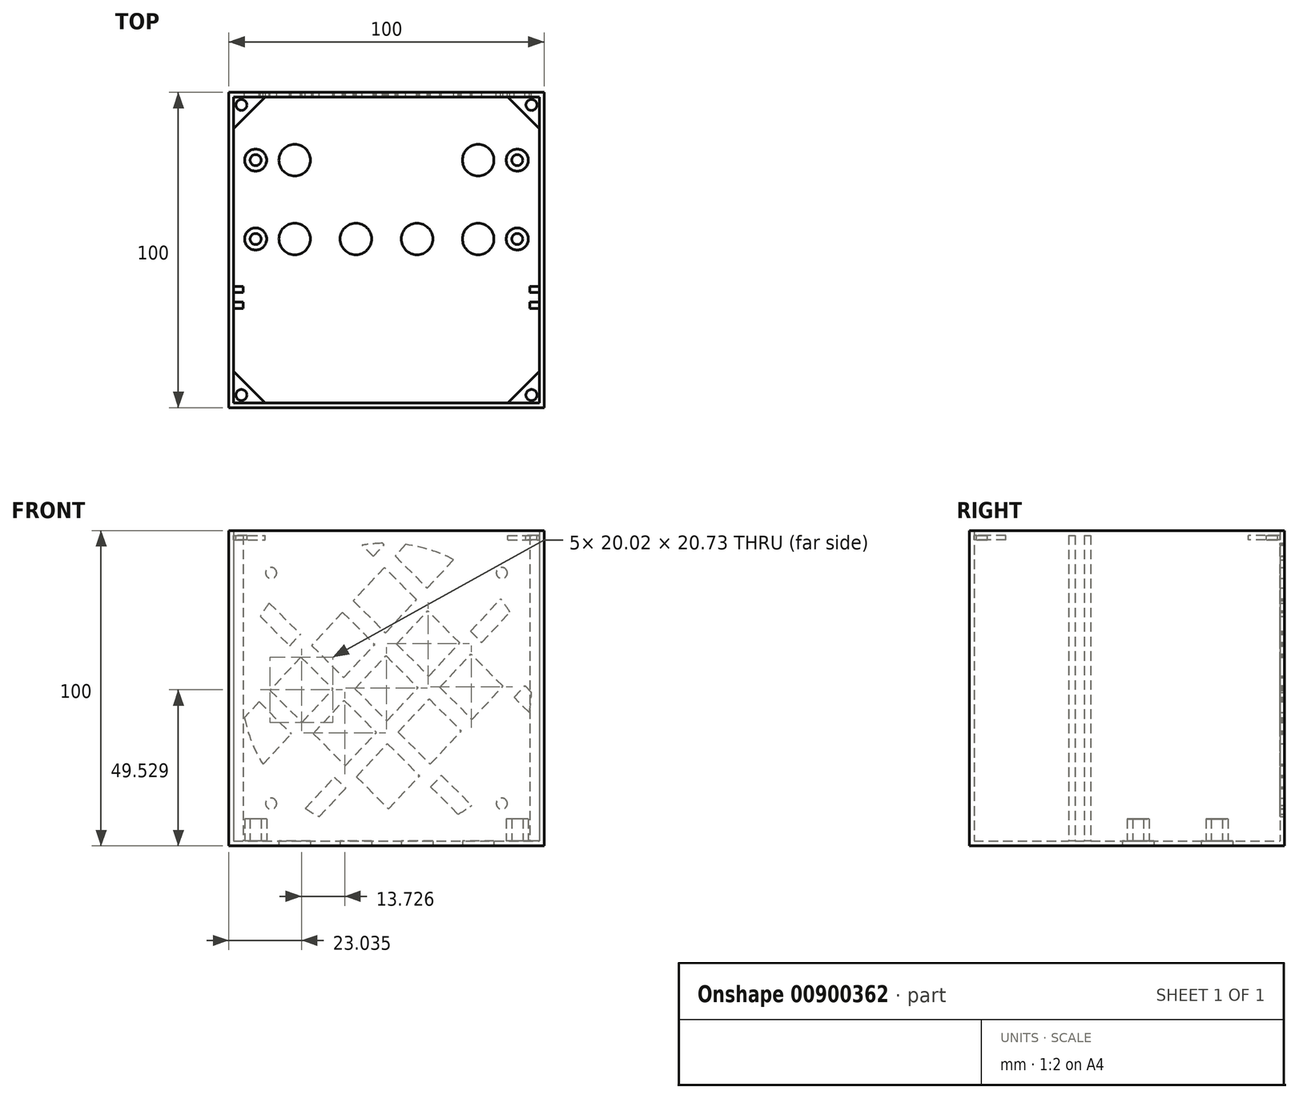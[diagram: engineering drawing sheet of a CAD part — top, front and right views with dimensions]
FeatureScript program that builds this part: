
annotation { "Feature Type Name" : "Feature", "Feature Type Description" : "" }
export const myFeature = defineFeature(function(context is Context, id is Id, definition is map)
    precondition{}
    {
        {
            var Q0;
            Q0=qCreatedBy(makeId("Top.planeOp"),FACE);
            var sketch = newSketch(context, id + "F0", { "sketchPlane" : qUnion([Q0])});
            skLineSegment(sketch, "E0.bottom", {"start": v(0, 0) * mm, "end": v(100, 0) * mm});
            skLineSegment(sketch, "E0.top", {"start": v(0, 100) * mm, "end": v(100, 100) * mm});
            skLineSegment(sketch, "E0.left", {"start": v(0, 0) * mm, "end": v(0, 100) * mm});
            skLineSegment(sketch, "E0.right", {"start": v(100, 0) * mm, "end": v(100, 100) * mm});
            skLineSegment(sketch, "E1.bottom", {"start": v(1.5, 1.5) * mm, "end": v(98.5, 1.5) * mm});
            skLineSegment(sketch, "E1.top", {"start": v(1.5, 98.5) * mm, "end": v(98.5, 98.5) * mm});
            skLineSegment(sketch, "E1.left", {"start": v(1.5, 1.5) * mm, "end": v(1.5, 98.5) * mm});
            skLineSegment(sketch, "E1.right", {"start": v(98.5, 1.5) * mm, "end": v(98.5, 98.5) * mm});
            skCircle(sketch, "E2", {"center": v(40.3, 53.5) * mm, "radius": 5 * mm});
            skCircle(sketch, "E3", {"center": v(59.7, 53.5) * mm, "radius": 5 * mm});
            skCircle(sketch, "E4", {"center": v(79.1, 53.5) * mm, "radius": 5 * mm});
            skCircle(sketch, "E5", {"center": v(20.9, 53.5) * mm, "radius": 5 * mm});
            skCircle(sketch, "E6", {"center": v(20.9, 78.5) * mm, "radius": 5 * mm});
            skCircle(sketch, "E7", {"center": v(79.1, 78.5) * mm, "radius": 5 * mm});
            skLineSegment(sketch, "E8", {"start": v(1.5, 53.5) * mm, "end": v(98.5, 53.5) * mm, "construction": true});
            skLineSegment(sketch, "E9.bottom", {"start": v(1.5, 38.5) * mm, "end": v(4.5, 38.5) * mm});
            skLineSegment(sketch, "E9.top", {"start": v(1.5, 36.5) * mm, "end": v(4.5, 36.5) * mm});
            skLineSegment(sketch, "E9.left", {"start": v(1.5, 38.5) * mm, "end": v(1.5, 36.5) * mm});
            skLineSegment(sketch, "E9.right", {"start": v(4.5, 38.5) * mm, "end": v(4.5, 36.5) * mm});
            skLineSegment(sketch, "E10.bottom", {"start": v(1.5, 33.5) * mm, "end": v(4.5, 33.5) * mm});
            skLineSegment(sketch, "E10.top", {"start": v(1.5, 31.5) * mm, "end": v(4.5, 31.5) * mm});
            skLineSegment(sketch, "E10.left", {"start": v(1.5, 33.5) * mm, "end": v(1.5, 31.5) * mm});
            skLineSegment(sketch, "E10.right", {"start": v(4.5, 33.5) * mm, "end": v(4.5, 31.5) * mm});
            skLineSegment(sketch, "E11.bottom", {"start": v(98.5, 38.5) * mm, "end": v(95.5, 38.5) * mm});
            skLineSegment(sketch, "E11.top", {"start": v(98.5, 36.5) * mm, "end": v(95.5, 36.5) * mm});
            skLineSegment(sketch, "E11.left", {"start": v(98.5, 38.5) * mm, "end": v(98.5, 36.5) * mm});
            skLineSegment(sketch, "E11.right", {"start": v(95.5, 38.5) * mm, "end": v(95.5, 36.5) * mm});
            skLineSegment(sketch, "E12.bottom", {"start": v(98.5, 33.5) * mm, "end": v(95.5, 33.5) * mm});
            skLineSegment(sketch, "E12.top", {"start": v(98.5, 31.5) * mm, "end": v(95.5, 31.5) * mm});
            skLineSegment(sketch, "E12.left", {"start": v(98.5, 33.5) * mm, "end": v(98.5, 31.5) * mm});
            skLineSegment(sketch, "E12.right", {"start": v(95.5, 33.5) * mm, "end": v(95.5, 31.5) * mm});
            skSolve(sketch);
        }
        {
            var Q0;
            Q0 = qSketchRegion(id + "F0", true);
            var Q1;
            Q1=makeQuery(id+"F0.imprint","IMPRINT",FACE,{"disambiguationData":[TD([[makeQuery(id+"F0.imprint","IMPRINT",EDGE,{"derivedFrom":sQuery(id+"F0.wireOp",EDGE,"E1.bottom")}),1.0]])]});
            var Q2;
            Q2=makeQuery(id+"F0.imprint","IMPRINT",FACE,{"disambiguationData":[TD([[makeQuery(id+"F0.imprint","IMPRINT",EDGE,{"derivedFrom":sQuery(id+"F0.wireOp",EDGE,"E9.bottom")}),-1.0]])]});
            var Q3;
            Q3=makeQuery(id+"F0.imprint","IMPRINT",FACE,{"disambiguationData":[TD([[makeQuery(id+"F0.imprint","IMPRINT",EDGE,{"derivedFrom":sQuery(id+"F0.wireOp",EDGE,"E10.bottom")}),-1.0]])]});
            var Q4;
            Q4=makeQuery(id+"F0.imprint","IMPRINT",FACE,{"disambiguationData":[TD([[makeQuery(id+"F0.imprint","IMPRINT",EDGE,{"derivedFrom":sQuery(id+"F0.wireOp",EDGE,"E11.bottom")}),1.0]])]});
            var Q5;
            Q5=makeQuery(id+"F0.imprint","IMPRINT",FACE,{"disambiguationData":[TD([[makeQuery(id+"F0.imprint","IMPRINT",EDGE,{"derivedFrom":sQuery(id+"F0.wireOp",EDGE,"E12.bottom")}),1.0]])]});
            extrude(context, id + "F1", {"entities" : qUnion([Q0, Q1, Q2, Q3, Q4, Q5]), "depth" : 1.5 * mm, "offsetDistance" : 25 * mm});
        }
        {
            var Q0;
            Q0=makeQuery(id+"F1.opExtrude","CAP_FACE",FACE,{"disambiguationData":[OSD([sQuery(id+"F0.wireOp",EDGE,"E0.bottom"),sQuery(id+"F0.wireOp",EDGE,"E0.top"),sQuery(id+"F0.wireOp",EDGE,"E0.left"),sQuery(id+"F0.wireOp",EDGE,"E0.right"),sQuery(id+"F0.wireOp",EDGE,"E2"),sQuery(id+"F0.wireOp",EDGE,"E3"),sQuery(id+"F0.wireOp",EDGE,"E4"),sQuery(id+"F0.wireOp",EDGE,"E5"),sQuery(id+"F0.wireOp",EDGE,"E6"),sQuery(id+"F0.wireOp",EDGE,"E7")])],"isStart":false});
            var sketch = newSketch(context, id + "F2", { "sketchPlane" : qUnion([Q0])});
            skLineSegment(sketch, "E13.bottom", {"start": v(0, 0) * mm, "end": v(100, 0) * mm});
            skLineSegment(sketch, "E13.top", {"start": v(0, 100) * mm, "end": v(100, 100) * mm});
            skLineSegment(sketch, "E13.left", {"start": v(0, 0) * mm, "end": v(0, 100) * mm});
            skLineSegment(sketch, "E13.right", {"start": v(100, 0) * mm, "end": v(100, 100) * mm});
            skLineSegment(sketch, "E14.bottom", {"start": v(1.5, 1.5) * mm, "end": v(98.5, 1.5) * mm});
            skLineSegment(sketch, "E14.top", {"start": v(1.5, 98.5) * mm, "end": v(98.5, 98.5) * mm});
            skLineSegment(sketch, "E14.left", {"start": v(1.5, 1.5) * mm, "end": v(1.5, 98.5) * mm});
            skLineSegment(sketch, "E14.right", {"start": v(98.5, 1.5) * mm, "end": v(98.5, 98.5) * mm});
            skCircle(sketch, "E15", {"center": v(40.3, 53.5) * mm, "radius": 5 * mm});
            skCircle(sketch, "E16", {"center": v(59.7, 53.5) * mm, "radius": 5 * mm});
            skCircle(sketch, "E17", {"center": v(79.1, 53.5) * mm, "radius": 5 * mm});
            skCircle(sketch, "E18", {"center": v(20.9, 53.5) * mm, "radius": 5 * mm});
            skCircle(sketch, "E19", {"center": v(20.9, 78.5) * mm, "radius": 5 * mm});
            skCircle(sketch, "E20", {"center": v(79.1, 78.5) * mm, "radius": 5 * mm});
            skLineSegment(sketch, "E21", {"start": v(1.5, 53.5) * mm, "end": v(98.5, 53.5) * mm, "construction": true});
            skLineSegment(sketch, "E22.bottom", {"start": v(1.5, 38.5) * mm, "end": v(4.5, 38.5) * mm});
            skLineSegment(sketch, "E22.top", {"start": v(1.5, 36.5) * mm, "end": v(4.5, 36.5) * mm});
            skLineSegment(sketch, "E22.left", {"start": v(1.5, 38.5) * mm, "end": v(1.5, 36.5) * mm});
            skLineSegment(sketch, "E22.right", {"start": v(4.5, 38.5) * mm, "end": v(4.5, 36.5) * mm});
            skLineSegment(sketch, "E23.bottom", {"start": v(1.5, 33.5) * mm, "end": v(4.5, 33.5) * mm});
            skLineSegment(sketch, "E23.top", {"start": v(1.5, 31.5) * mm, "end": v(4.5, 31.5) * mm});
            skLineSegment(sketch, "E23.left", {"start": v(1.5, 33.5) * mm, "end": v(1.5, 31.5) * mm});
            skLineSegment(sketch, "E23.right", {"start": v(4.5, 33.5) * mm, "end": v(4.5, 31.5) * mm});
            skLineSegment(sketch, "E24.bottom", {"start": v(98.5, 38.5) * mm, "end": v(95.5, 38.5) * mm});
            skLineSegment(sketch, "E24.top", {"start": v(98.5, 36.5) * mm, "end": v(95.5, 36.5) * mm});
            skLineSegment(sketch, "E24.left", {"start": v(98.5, 38.5) * mm, "end": v(98.5, 36.5) * mm});
            skLineSegment(sketch, "E24.right", {"start": v(95.5, 38.5) * mm, "end": v(95.5, 36.5) * mm});
            skLineSegment(sketch, "E25.bottom", {"start": v(98.5, 33.5) * mm, "end": v(95.5, 33.5) * mm});
            skLineSegment(sketch, "E25.top", {"start": v(98.5, 31.5) * mm, "end": v(95.5, 31.5) * mm});
            skLineSegment(sketch, "E25.left", {"start": v(98.5, 33.5) * mm, "end": v(98.5, 31.5) * mm});
            skLineSegment(sketch, "E25.right", {"start": v(95.5, 33.5) * mm, "end": v(95.5, 31.5) * mm});
            skCircle(sketch, "E26", {"center": v(8.5, 53.5) * mm, "radius": 1.75 * mm});
            skCircle(sketch, "E27", {"center": v(8.5, 53.5) * mm, "radius": 3.5 * mm});
            skCircle(sketch, "E28", {"center": v(91.5, 53.5) * mm, "radius": 1.75 * mm});
            skCircle(sketch, "E29", {"center": v(91.5, 53.5) * mm, "radius": 3.5 * mm});
            skLineSegment(sketch, "E30", {"start": v(1.5, 78.5) * mm, "end": v(98.5, 78.5) * mm, "construction": true});
            skCircle(sketch, "E31", {"center": v(8.5, 78.5) * mm, "radius": 1.75 * mm});
            skCircle(sketch, "E32", {"center": v(8.5, 78.5) * mm, "radius": 3.5 * mm});
            skCircle(sketch, "E33", {"center": v(91.5, 78.5) * mm, "radius": 1.75 * mm});
            skCircle(sketch, "E34", {"center": v(91.5, 78.5) * mm, "radius": 3.5 * mm});
            skSolve(sketch);
        }
        {
            var Q0;
            Q0=makeQuery(id+"F2.imprint","IMPRINT",FACE,{"disambiguationData":[TD([[makeQuery(id+"F2.imprint","IMPRINT",EDGE,{"derivedFrom":sQuery(id+"F2.wireOp",EDGE,"E13.bottom")}),1.0]])]});
            extrude(context, id + "F3", {"entities" : qUnion([Q0]), "operationType" : NewBodyOperationType.ADD, "depth" : 98.5 * mm, "offsetDistance" : 25 * mm});
        }
        {
            var Q0;
            Q0 = qSketchRegion(id + "F2", true);
            var Q1;
            Q1=makeQuery(id+"F2.imprint","IMPRINT",FACE,{"disambiguationData":[TD([[makeQuery(id+"F2.imprint","IMPRINT",EDGE,{"derivedFrom":sQuery(id+"F2.wireOp",EDGE,"E22.bottom")}),-1.0]])]});
            var Q2;
            Q2=makeQuery(id+"F2.imprint","IMPRINT",FACE,{"disambiguationData":[TD([[makeQuery(id+"F2.imprint","IMPRINT",EDGE,{"derivedFrom":sQuery(id+"F2.wireOp",EDGE,"E23.bottom")}),-1.0]])]});
            var Q3;
            Q3=makeQuery(id+"F2.imprint","IMPRINT",FACE,{"disambiguationData":[TD([[makeQuery(id+"F2.imprint","IMPRINT",EDGE,{"derivedFrom":sQuery(id+"F2.wireOp",EDGE,"E24.bottom")}),1.0]])]});
            var Q4;
            Q4=makeQuery(id+"F2.imprint","IMPRINT",FACE,{"disambiguationData":[TD([[makeQuery(id+"F2.imprint","IMPRINT",EDGE,{"derivedFrom":sQuery(id+"F2.wireOp",EDGE,"E25.bottom")}),1.0]])]});
            extrude(context, id + "F4", {"entities" : qUnion([Q0, Q1, Q2, Q3, Q4]), "operationType" : NewBodyOperationType.ADD, "depth" : 97 * mm, "offsetDistance" : 25 * mm});
        }
        {
            var Q0;
            Q0=makeQuery(id+"F3.boolean.opBoolean","MERGE",FACE,{"derivedFrom":[makeQuery(id+"F1.opExtrude","SWEPT_FACE",FACE,{"disambiguationData":[OSD([sQuery(id+"F0.wireOp",EDGE,"E0.top")])]}),makeQuery(id+"F3.opExtrude","SWEPT_FACE",FACE,{"disambiguationData":[OSD([sQuery(id+"F2.wireOp",EDGE,"E13.top")])]})]});
            var sketch = newSketch(context, id + "F5", { "sketchPlane" : qUnion([Q0])});
            skLineSegment(sketch, "E35.0", {"start": v(0, 0) * mm, "end": v(-100, 0) * mm});
            skLineSegment(sketch, "E36.0", {"start": v(0, 100) * mm, "end": v(-100, 100) * mm});
            skLineSegment(sketch, "E37", {"start": v(-50, 100) * mm, "end": v(-50, 0) * mm, "construction": true});
            skLineSegment(sketch, "E38", {"start": v(-100, 50) * mm, "end": v(0, 50) * mm, "construction": true});
            skCircle(sketch, "E39", {"center": v(-50, 50) * mm, "radius": 46 * mm});
            skLineSegment(sketch, "E40", {"start": v(-48.7, 95.98) * mm, "end": v(-95.98, 48.7) * mm});
            skLineSegment(sketch, "E41", {"start": v(-95.35, 42.27) * mm, "end": v(-42.27, 95.35) * mm});
            skLineSegment(sketch, "E42", {"start": v(-27.26, 89.99) * mm, "end": v(-89.99, 27.26) * mm});
            skLineSegment(sketch, "E43", {"start": v(-12.78, 77.03) * mm, "end": v(-77.03, 12.78) * mm});
            skLineSegment(sketch, "E44", {"start": v(-10.01, 72.74) * mm, "end": v(-72.74, 10.01) * mm});
            skLineSegment(sketch, "E45", {"start": v(-4.65, 57.73) * mm, "end": v(-57.73, 4.65) * mm});
            skLineSegment(sketch, "E46", {"start": v(-4.02, 51.3) * mm, "end": v(-51.3, 4.02) * mm});
            skLineSegment(sketch, "E47", {"start": v(-22.97, 87.22) * mm, "end": v(-87.22, 22.97) * mm});
            skLineSegment(sketch, "E48", {"start": v(-4.1, 47.1) * mm, "end": v(-49.69, 96) * mm});
            skLineSegment(sketch, "E49", {"start": v(-56.14, 95.59) * mm, "end": v(-4.95, 40.7) * mm});
            skLineSegment(sketch, "E50", {"start": v(-10.83, 25.88) * mm, "end": v(-71.32, 90.76) * mm});
            skLineSegment(sketch, "E51", {"start": v(-24.28, 11.86) * mm, "end": v(-86.25, 78.32) * mm});
            skLineSegment(sketch, "E52", {"start": v(-28.68, 9.24) * mm, "end": v(-89.17, 74.12) * mm});
            skLineSegment(sketch, "E53", {"start": v(-43.86, 4.41) * mm, "end": v(-95.05, 59.3) * mm});
            skLineSegment(sketch, "E54", {"start": v(-50.31, 4) * mm, "end": v(-95.9, 52.9) * mm});
            skLineSegment(sketch, "E55", {"start": v(-13.75, 21.68) * mm, "end": v(-75.72, 88.14) * mm});
            skLineSegment(sketch, "E56", {"start": v(0, 100) * mm, "end": v(-100, 0) * mm, "construction": true});
            skLineSegment(sketch, "E57", {"start": v(-100, 100) * mm, "end": v(0, 0) * mm, "construction": true});
            skCircle(sketch, "E58", {"center": v(-13.4, 86.6) * mm, "radius": 1.75 * mm});
            skCircle(sketch, "E59", {"center": v(-86.6, 86.6) * mm, "radius": 1.75 * mm});
            skCircle(sketch, "E60", {"center": v(-86.6, 13.4) * mm, "radius": 1.75 * mm});
            skCircle(sketch, "E61", {"center": v(-13.4, 13.4) * mm, "radius": 1.75 * mm});
            skSolve(sketch);
        }
        {
            var Q0;
            {var subQ0=sQuery(id+"F5.wireOp",EDGE,"E51");var subQ1=sQuery(id+"F5.wireOp",EDGE,"E39");var subQ2=makeQuery(id+"F5.imprint","INTERSECT",VERTEX,{"disambiguationData":[OD(1.0)],"derivedFrom":[subQ1,subQ0]});Q0=makeQuery(id+"F5.imprint","IMPRINT",FACE,{"disambiguationData":[TD([[makeQuery(id+"F5.imprint","IMPRINT",EDGE,{"disambiguationData":[TD([[subQ2,1.0]])],"derivedFrom":subQ1}),1.0]])]});}
            var Q1;
            {var subQ0=sQuery(id+"F5.wireOp",EDGE,"E49");var subQ1=sQuery(id+"F5.wireOp",EDGE,"E39");var subQ2=makeQuery(id+"F5.imprint","INTERSECT",VERTEX,{"disambiguationData":[OD(0.0)],"derivedFrom":[subQ1,subQ0]});Q1=makeQuery(id+"F5.imprint","IMPRINT",FACE,{"disambiguationData":[TD([[makeQuery(id+"F5.imprint","IMPRINT",EDGE,{"disambiguationData":[TD([[subQ2,-1.0]])],"derivedFrom":subQ1}),1.0]])]});}
            var Q2;
            {var subQ0=sQuery(id+"F5.wireOp",EDGE,"E41");var subQ1=sQuery(id+"F5.wireOp",EDGE,"E39");var subQ2=makeQuery(id+"F5.imprint","INTERSECT",VERTEX,{"disambiguationData":[OD(1.0)],"derivedFrom":[subQ1,subQ0]});Q2=makeQuery(id+"F5.imprint","IMPRINT",FACE,{"disambiguationData":[TD([[makeQuery(id+"F5.imprint","IMPRINT",EDGE,{"disambiguationData":[TD([[subQ2,1.0]])],"derivedFrom":subQ1}),1.0]])]});}
            var Q3;
            {var subQ0=sQuery(id+"F5.wireOp",EDGE,"E43");var subQ1=sQuery(id+"F5.wireOp",EDGE,"E39");var subQ2=makeQuery(id+"F5.imprint","INTERSECT",VERTEX,{"disambiguationData":[OD(0.0)],"derivedFrom":[subQ1,subQ0]});Q3=makeQuery(id+"F5.imprint","IMPRINT",FACE,{"disambiguationData":[TD([[makeQuery(id+"F5.imprint","IMPRINT",EDGE,{"disambiguationData":[TD([[subQ2,-1.0]])],"derivedFrom":subQ1}),1.0]])]});}
            var Q4;
            {var subQ0=sQuery(id+"F5.wireOp",EDGE,"E50");var subQ1=sQuery(id+"F5.wireOp",EDGE,"E41");var subQ2=makeQuery(id+"F5.imprint","INTERSECT",VERTEX,{"derivedFrom":[subQ1,subQ0]});Q4=makeQuery(id+"F5.imprint","IMPRINT",FACE,{"disambiguationData":[TD([[makeQuery(id+"F5.imprint","IMPRINT",EDGE,{"disambiguationData":[TD([[subQ2,-1.0]])],"derivedFrom":subQ1}),-1.0]])]});}
            var Q5;
            {var subQ0=sQuery(id+"F5.wireOp",EDGE,"E52");var subQ1=sQuery(id+"F5.wireOp",EDGE,"E39");var subQ2=makeQuery(id+"F5.imprint","INTERSECT",VERTEX,{"disambiguationData":[OD(1.0)],"derivedFrom":[subQ1,subQ0]});Q5=makeQuery(id+"F5.imprint","IMPRINT",FACE,{"disambiguationData":[TD([[makeQuery(id+"F5.imprint","IMPRINT",EDGE,{"disambiguationData":[TD([[subQ2,-1.0]])],"derivedFrom":subQ1}),1.0]])]});}
            var Q6;
            {var subQ0=sQuery(id+"F5.wireOp",EDGE,"E51");var subQ1=sQuery(id+"F5.wireOp",EDGE,"E41");var subQ2=makeQuery(id+"F5.imprint","INTERSECT",VERTEX,{"derivedFrom":[subQ1,subQ0]});Q6=makeQuery(id+"F5.imprint","IMPRINT",FACE,{"disambiguationData":[TD([[makeQuery(id+"F5.imprint","IMPRINT",EDGE,{"disambiguationData":[TD([[subQ2,-1.0]])],"derivedFrom":subQ1}),-1.0]])]});}
            var Q7;
            {var subQ0=sQuery(id+"F5.wireOp",EDGE,"E49");var subQ1=sQuery(id+"F5.wireOp",EDGE,"E43");var subQ2=makeQuery(id+"F5.imprint","INTERSECT",VERTEX,{"derivedFrom":[subQ1,subQ0]});Q7=makeQuery(id+"F5.imprint","IMPRINT",FACE,{"disambiguationData":[TD([[makeQuery(id+"F5.imprint","IMPRINT",EDGE,{"disambiguationData":[TD([[subQ2,-1.0]])],"derivedFrom":subQ1}),-1.0]])]});}
            var Q8;
            {var subQ0=sQuery(id+"F5.wireOp",EDGE,"E44");var subQ1=sQuery(id+"F5.wireOp",EDGE,"E39");var subQ2=makeQuery(id+"F5.imprint","INTERSECT",VERTEX,{"disambiguationData":[OD(0.0)],"derivedFrom":[subQ1,subQ0]});Q8=makeQuery(id+"F5.imprint","IMPRINT",FACE,{"disambiguationData":[TD([[makeQuery(id+"F5.imprint","IMPRINT",EDGE,{"disambiguationData":[TD([[subQ2,1.0]])],"derivedFrom":subQ1}),1.0]])]});}
            var Q9;
            {var subQ0=sQuery(id+"F5.wireOp",EDGE,"E49");var subQ1=sQuery(id+"F5.wireOp",EDGE,"E44");var subQ2=makeQuery(id+"F5.imprint","INTERSECT",VERTEX,{"derivedFrom":[subQ1,subQ0]});Q9=makeQuery(id+"F5.imprint","IMPRINT",FACE,{"disambiguationData":[TD([[makeQuery(id+"F5.imprint","IMPRINT",EDGE,{"disambiguationData":[TD([[subQ2,-1.0]])],"derivedFrom":subQ1}),1.0]])]});}
            var Q10;
            {var subQ0=sQuery(id+"F5.wireOp",EDGE,"E55");var subQ1=sQuery(id+"F5.wireOp",EDGE,"E43");var subQ2=makeQuery(id+"F5.imprint","INTERSECT",VERTEX,{"derivedFrom":[subQ1,subQ0]});Q10=makeQuery(id+"F5.imprint","IMPRINT",FACE,{"disambiguationData":[TD([[makeQuery(id+"F5.imprint","IMPRINT",EDGE,{"disambiguationData":[TD([[subQ2,-1.0]])],"derivedFrom":subQ1}),-1.0]])]});}
            var Q11;
            {var subQ0=sQuery(id+"F5.wireOp",EDGE,"E53");var subQ1=sQuery(id+"F5.wireOp",EDGE,"E41");var subQ2=makeQuery(id+"F5.imprint","INTERSECT",VERTEX,{"derivedFrom":[subQ1,subQ0]});Q11=makeQuery(id+"F5.imprint","IMPRINT",FACE,{"disambiguationData":[TD([[makeQuery(id+"F5.imprint","IMPRINT",EDGE,{"disambiguationData":[TD([[subQ2,-1.0]])],"derivedFrom":subQ1}),-1.0]])]});}
            var Q12;
            {var subQ0=sQuery(id+"F5.wireOp",EDGE,"E41");var subQ1=sQuery(id+"F5.wireOp",EDGE,"E39");var subQ2=makeQuery(id+"F5.imprint","INTERSECT",VERTEX,{"disambiguationData":[OD(0.0)],"derivedFrom":[subQ1,subQ0]});Q12=makeQuery(id+"F5.imprint","IMPRINT",FACE,{"disambiguationData":[TD([[makeQuery(id+"F5.imprint","IMPRINT",EDGE,{"disambiguationData":[TD([[subQ2,-1.0]])],"derivedFrom":subQ1}),1.0]])]});}
            var Q13;
            {var subQ0=sQuery(id+"F5.wireOp",EDGE,"E52");var subQ1=sQuery(id+"F5.wireOp",EDGE,"E43");var subQ2=makeQuery(id+"F5.imprint","INTERSECT",VERTEX,{"derivedFrom":[subQ1,subQ0]});Q13=makeQuery(id+"F5.imprint","IMPRINT",FACE,{"disambiguationData":[TD([[makeQuery(id+"F5.imprint","IMPRINT",EDGE,{"disambiguationData":[TD([[subQ2,-1.0]])],"derivedFrom":subQ1}),-1.0]])]});}
            var Q14;
            {var subQ0=sQuery(id+"F5.wireOp",EDGE,"E55");var subQ1=sQuery(id+"F5.wireOp",EDGE,"E44");var subQ2=makeQuery(id+"F5.imprint","INTERSECT",VERTEX,{"derivedFrom":[subQ1,subQ0]});Q14=makeQuery(id+"F5.imprint","IMPRINT",FACE,{"disambiguationData":[TD([[makeQuery(id+"F5.imprint","IMPRINT",EDGE,{"disambiguationData":[TD([[subQ2,-1.0]])],"derivedFrom":subQ1}),1.0]])]});}
            var Q15;
            {var subQ0=sQuery(id+"F5.wireOp",EDGE,"E49");var subQ1=sQuery(id+"F5.wireOp",EDGE,"E39");var subQ2=makeQuery(id+"F5.imprint","INTERSECT",VERTEX,{"disambiguationData":[OD(1.0)],"derivedFrom":[subQ1,subQ0]});Q15=makeQuery(id+"F5.imprint","IMPRINT",FACE,{"disambiguationData":[TD([[makeQuery(id+"F5.imprint","IMPRINT",EDGE,{"disambiguationData":[TD([[subQ2,1.0]])],"derivedFrom":subQ1}),1.0]])]});}
            var Q16;
            {var subQ0=sQuery(id+"F5.wireOp",EDGE,"E51");var subQ1=sQuery(id+"F5.wireOp",EDGE,"E39");var subQ2=makeQuery(id+"F5.imprint","INTERSECT",VERTEX,{"disambiguationData":[OD(0.0)],"derivedFrom":[subQ1,subQ0]});Q16=makeQuery(id+"F5.imprint","IMPRINT",FACE,{"disambiguationData":[TD([[makeQuery(id+"F5.imprint","IMPRINT",EDGE,{"disambiguationData":[TD([[subQ2,-1.0]])],"derivedFrom":subQ1}),1.0]])]});}
            var Q17;
            {var subQ0=sQuery(id+"F5.wireOp",EDGE,"E52");var subQ1=sQuery(id+"F5.wireOp",EDGE,"E44");var subQ2=makeQuery(id+"F5.imprint","INTERSECT",VERTEX,{"derivedFrom":[subQ1,subQ0]});Q17=makeQuery(id+"F5.imprint","IMPRINT",FACE,{"disambiguationData":[TD([[makeQuery(id+"F5.imprint","IMPRINT",EDGE,{"disambiguationData":[TD([[subQ2,-1.0]])],"derivedFrom":subQ1}),1.0]])]});}
            var Q18;
            {var subQ0=sQuery(id+"F5.wireOp",EDGE,"E43");var subQ1=sQuery(id+"F5.wireOp",EDGE,"E39");var subQ2=makeQuery(id+"F5.imprint","INTERSECT",VERTEX,{"disambiguationData":[OD(1.0)],"derivedFrom":[subQ1,subQ0]});Q18=makeQuery(id+"F5.imprint","IMPRINT",FACE,{"disambiguationData":[TD([[makeQuery(id+"F5.imprint","IMPRINT",EDGE,{"disambiguationData":[TD([[subQ2,1.0]])],"derivedFrom":subQ1}),1.0]])]});}
            var Q19;
            {var subQ0=sQuery(id+"F5.wireOp",EDGE,"E44");var subQ1=sQuery(id+"F5.wireOp",EDGE,"E39");var subQ2=makeQuery(id+"F5.imprint","INTERSECT",VERTEX,{"disambiguationData":[OD(1.0)],"derivedFrom":[subQ1,subQ0]});Q19=makeQuery(id+"F5.imprint","IMPRINT",FACE,{"disambiguationData":[TD([[makeQuery(id+"F5.imprint","IMPRINT",EDGE,{"disambiguationData":[TD([[subQ2,-1.0]])],"derivedFrom":subQ1}),1.0]])]});}
            var Q20;
            {var subQ0=sQuery(id+"F5.wireOp",EDGE,"E52");var subQ1=sQuery(id+"F5.wireOp",EDGE,"E39");var subQ2=makeQuery(id+"F5.imprint","INTERSECT",VERTEX,{"disambiguationData":[OD(0.0)],"derivedFrom":[subQ1,subQ0]});Q20=makeQuery(id+"F5.imprint","IMPRINT",FACE,{"disambiguationData":[TD([[makeQuery(id+"F5.imprint","IMPRINT",EDGE,{"disambiguationData":[TD([[subQ2,1.0]])],"derivedFrom":subQ1}),1.0]])]});}
            var Q21;
            Q21=makeQuery(id+"F5.imprint","IMPRINT",FACE,{"disambiguationData":[TD([[makeQuery(id+"F5.imprint","IMPRINT",EDGE,{"derivedFrom":sQuery(id+"F5.wireOp",EDGE,"E59")}),1.0]])]});
            var Q22;
            Q22=makeQuery(id+"F5.imprint","IMPRINT",FACE,{"disambiguationData":[TD([[makeQuery(id+"F5.imprint","IMPRINT",EDGE,{"derivedFrom":sQuery(id+"F5.wireOp",EDGE,"E58")}),1.0]])]});
            var Q23;
            Q23=makeQuery(id+"F5.imprint","IMPRINT",FACE,{"disambiguationData":[TD([[makeQuery(id+"F5.imprint","IMPRINT",EDGE,{"derivedFrom":sQuery(id+"F5.wireOp",EDGE,"E61")}),1.0]])]});
            var Q24;
            Q24=makeQuery(id+"F5.imprint","IMPRINT",FACE,{"disambiguationData":[TD([[makeQuery(id+"F5.imprint","IMPRINT",EDGE,{"derivedFrom":sQuery(id+"F5.wireOp",EDGE,"E60")}),1.0]])]});
            extrude(context, id + "F6", {"entities" : qUnion([Q0, Q1, Q2, Q3, Q4, Q5, Q6, Q7, Q8, Q9, Q10, Q11, Q12, Q13, Q14, Q15, Q16, Q17, Q18, Q19, Q20, Q21, Q22, Q23, Q24]), "operationType" : NewBodyOperationType.REMOVE, "depth" : -1.5 * mm, "offsetDistance" : 25 * mm});
        }
        {
            var Q0;
            Q0=makeQuery(id+"F3.opExtrude","CAP_FACE",FACE,{"disambiguationData":[OSD([sQuery(id+"F2.wireOp",EDGE,"E13.bottom"),sQuery(id+"F2.wireOp",EDGE,"E13.top"),sQuery(id+"F2.wireOp",EDGE,"E13.left"),sQuery(id+"F2.wireOp",EDGE,"E13.right"),sQuery(id+"F2.wireOp",EDGE,"E14.bottom"),sQuery(id+"F2.wireOp",EDGE,"E14.top"),sQuery(id+"F2.wireOp",EDGE,"E14.left"),sQuery(id+"F2.wireOp",EDGE,"E14.right")])],"isStart":false});
            var sketch = newSketch(context, id + "F7", { "sketchPlane" : qUnion([Q0])});
            skLineSegment(sketch, "E62.0", {"start": v(1.5, 98.5) * mm, "end": v(98.5, 98.5) * mm});
            skLineSegment(sketch, "E62.1", {"start": v(1.5, 1.5) * mm, "end": v(1.5, 98.5) * mm});
            skLineSegment(sketch, "E62.2", {"start": v(98.5, 1.5) * mm, "end": v(98.5, 98.5) * mm});
            skLineSegment(sketch, "E62.3", {"start": v(1.5, 1.5) * mm, "end": v(98.5, 1.5) * mm});
            skLineSegment(sketch, "E63", {"start": v(11.5, 98.5) * mm, "end": v(1.5, 88.5) * mm});
            skLineSegment(sketch, "E64", {"start": v(1.5, 98.5) * mm, "end": v(6.5, 93.5) * mm, "construction": true});
            skPoint(sketch, "E65", {"position": v(4, 96) * mm});
            skCircle(sketch, "E66", {"center": v(4, 96) * mm, "radius": 1.75 * mm});
            skLineSegment(sketch, "E67", {"start": v(1.5, 98.5) * mm, "end": v(1.5, 88.5) * mm});
            skLineSegment(sketch, "E68", {"start": v(1.5, 98.5) * mm, "end": v(11.5, 98.5) * mm});
            skLineSegment(sketch, "E69", {"start": v(88.5, 1.5) * mm, "end": v(98.5, 11.5) * mm});
            skLineSegment(sketch, "E70", {"start": v(98.5, 1.5) * mm, "end": v(93.5, 6.5) * mm, "construction": true});
            skPoint(sketch, "E71", {"position": v(96, 4) * mm});
            skCircle(sketch, "E72", {"center": v(96, 4) * mm, "radius": 1.75 * mm});
            skLineSegment(sketch, "E73", {"start": v(1.5, 11.5) * mm, "end": v(11.5, 1.5) * mm});
            skLineSegment(sketch, "E74", {"start": v(1.5, 1.5) * mm, "end": v(6.5, 6.5) * mm, "construction": true});
            skPoint(sketch, "E75", {"position": v(4, 4) * mm});
            skCircle(sketch, "E76", {"center": v(4, 4) * mm, "radius": 1.75 * mm});
            skLineSegment(sketch, "E77", {"start": v(98.5, 88.5) * mm, "end": v(88.5, 98.5) * mm});
            skLineSegment(sketch, "E78", {"start": v(98.5, 98.5) * mm, "end": v(93.5, 93.5) * mm, "construction": true});
            skPoint(sketch, "E79", {"position": v(96, 96) * mm});
            skCircle(sketch, "E80", {"center": v(96, 96) * mm, "radius": 1.75 * mm});
            skSolve(sketch);
        }
        {
            var Q0;
            Q0=makeQuery(id+"F7.imprint","IMPRINT",FACE,{"disambiguationData":[TD([[makeQuery(id+"F7.imprint","IMPRINT",EDGE,{"derivedFrom":sQuery(id+"F7.wireOp",EDGE,"E63")}),-1.0]])]});
            var Q1;
            {var subQ3=sQuery(id+"F7.wireOp",EDGE,"E77");Q1=makeQuery(id+"F7.imprint","IMPRINT",FACE,{"disambiguationData":[TD([[makeQuery(id+"F7.imprint","IMPRINT",EDGE,{"derivedFrom":subQ3}),-1.0]])]});}
            var Q2;
            {var subQ3=sQuery(id+"F7.wireOp",EDGE,"E69");Q2=makeQuery(id+"F7.imprint","IMPRINT",FACE,{"disambiguationData":[TD([[makeQuery(id+"F7.imprint","IMPRINT",EDGE,{"derivedFrom":subQ3}),-1.0]])]});}
            var Q3;
            {var subQ3=sQuery(id+"F7.wireOp",EDGE,"E73");Q3=makeQuery(id+"F7.imprint","IMPRINT",FACE,{"disambiguationData":[TD([[makeQuery(id+"F7.imprint","IMPRINT",EDGE,{"derivedFrom":subQ3}),-1.0]])]});}
            extrude(context, id + "F8", {"entities" : qUnion([Q0, Q1, Q2, Q3]), "depth" : -3 * mm, "offsetDistance" : 25 * mm});
        }
        {
            var Q0;
            Q0=makeQuery(id+"F8.opExtrude","CAP_FACE",FACE,{"disambiguationData":[OSD([sQuery(id+"F7.wireOp",EDGE,"E63"),sQuery(id+"F7.wireOp",EDGE,"E66"),sQuery(id+"F7.wireOp",EDGE,"E67"),sQuery(id+"F7.wireOp",EDGE,"E68")])],"isStart":true});
            var Q1;
            Q1=makeQuery(id+"F8.opExtrude","CAP_FACE",FACE,{"disambiguationData":[OSD([sQuery(id+"F7.wireOp",EDGE,"E62.0"),sQuery(id+"F7.wireOp",EDGE,"E62.2"),sQuery(id+"F7.wireOp",EDGE,"E77"),sQuery(id+"F7.wireOp",EDGE,"E80")])],"isStart":true});
            var Q2;
            Q2=makeQuery(id+"F8.opExtrude","CAP_FACE",FACE,{"disambiguationData":[OSD([sQuery(id+"F7.wireOp",EDGE,"E62.2"),sQuery(id+"F7.wireOp",EDGE,"E62.3"),sQuery(id+"F7.wireOp",EDGE,"E69"),sQuery(id+"F7.wireOp",EDGE,"E72")])],"isStart":true});
            var Q3;
            Q3=makeQuery(id+"F8.opExtrude","CAP_FACE",FACE,{"disambiguationData":[OSD([sQuery(id+"F7.wireOp",EDGE,"E62.1"),sQuery(id+"F7.wireOp",EDGE,"E62.3"),sQuery(id+"F7.wireOp",EDGE,"E73"),sQuery(id+"F7.wireOp",EDGE,"E76")])],"isStart":true});
            extrude(context, id + "F9", {"entities" : qUnion([Q0, Q1, Q2, Q3]), "operationType" : NewBodyOperationType.REMOVE, "oppositeDirection" : true, "depth" : 1.5 * mm, "offsetDistance" : 25 * mm});
        }
        {
            var Q0;
            Q0=makeQuery(id+"F2.imprint","IMPRINT",FACE,{"disambiguationData":[TD([[makeQuery(id+"F2.imprint","IMPRINT",EDGE,{"derivedFrom":sQuery(id+"F2.wireOp",EDGE,"E31")}),-1.0]])]});
            var Q1;
            Q1=makeQuery(id+"F2.imprint","IMPRINT",FACE,{"disambiguationData":[TD([[makeQuery(id+"F2.imprint","IMPRINT",EDGE,{"derivedFrom":sQuery(id+"F2.wireOp",EDGE,"E33")}),-1.0]])]});
            var Q2;
            Q2=makeQuery(id+"F2.imprint","IMPRINT",FACE,{"disambiguationData":[TD([[makeQuery(id+"F2.imprint","IMPRINT",EDGE,{"derivedFrom":sQuery(id+"F2.wireOp",EDGE,"E28")}),-1.0]])]});
            var Q3;
            Q3=makeQuery(id+"F2.imprint","IMPRINT",FACE,{"disambiguationData":[TD([[makeQuery(id+"F2.imprint","IMPRINT",EDGE,{"derivedFrom":sQuery(id+"F2.wireOp",EDGE,"E26")}),-1.0]])]});
            extrude(context, id + "F10", {"entities" : qUnion([Q0, Q1, Q2, Q3]), "operationType" : NewBodyOperationType.ADD, "depth" : 7 * mm, "offsetDistance" : 25 * mm});
        }
    });
